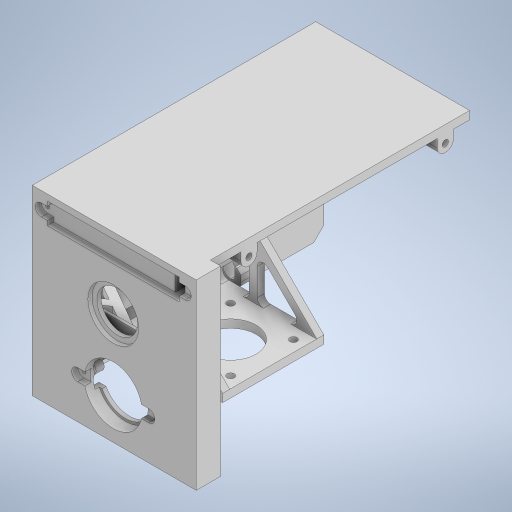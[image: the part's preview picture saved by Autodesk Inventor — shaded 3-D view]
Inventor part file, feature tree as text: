
AUTODESK INVENTOR PART (.ipt)
format: ipt  version: 2023 (Build 270158000, 158)  size: 762,368 bytes
history: native  units: mm
features: extrude x30, sketch x27, fillet x8, chamfer x7, other x6, mirror x2, revolve x2
ambient origin geometry x8: Origin, YZ Plane, XZ Plane, XY Plane, X Axis, Y Axis, Z Axis, Center Point
bodies: Body1 (feature_tree)
feature tree (82):
  other  "솔리드1"
  sketch  "스케치1"
  extrude  "돌출1"  Depth=90.0mm
  extrude  "돌출2"  Depth=140.0mm
  extrude  "돌출3"  Depth=4.0mm TaperAngle=0.0deg
  extrude  "돌출5"  Depth=72.0mm TaperAngle=0.0deg
  extrude  "돌출6"  Depth=4.0mm
  other  "작업 평면1"
  mirror  "미러1"
  extrude  "돌출7"  Depth=4.0mm
  extrude  "돌출8"  Depth=10.0mm
  extrude  "돌출9"  Depth=10.0mm
  extrude  "돌출10"  Depth=10.0mm
  extrude  "돌출11"  Depth=10.0mm
  sketch  "스케치11"
  extrude  "돌출12"  Depth=4.0mm
  extrude  "돌출13"  Depth=10.0mm TaperAngle=0.0deg
  extrude  "돌출14"  Depth=6.0mm
  chamfer  "모따기2"  Distance=36.0mm
  chamfer  "모따기3"  Distance=8.0mm
  extrude  "돌출15"  Depth=50.0mm
  fillet  "모깎기2"  Radius=10.0mm
  other  "작업 평면2"
  sketch  "스케치17"
  revolve  "회전1"
  revolve  "회전2"
  extrude  "돌출16"  Depth=46.0mm TaperAngle=0.0deg
  sketch  "스케치19"
  extrude  "돌출17"  Depth=30.0mm
  extrude  "돌출18"  TaperAngle=30.0deg  [1 undecoded]
  extrude  "돌출19"  Depth=4.0mm
  fillet  "모깎기3"  Radius=2.0mm
  other  "작업 평면3"
  extrude  "돌출20"  Depth=2.0mm
  extrude  "돌출21"  Depth=4.0mm TaperAngle=0.0deg
  extrude  "돌출22"  Depth=2.0mm
  other  "작업 평면4"
  fillet  "모깎기4"  Radius=40.0mm
  mirror  "미러2"
  chamfer  "모따기4"  Distance=20.0mm
  extrude  "돌출23"  Depth=20.0mm
  extrude  "돌출24"  Depth=36.0mm
  chamfer  "모따기5"  Distance=20.0mm
  extrude  "돌출25"  Depth=20.0mm TaperAngle=0.0deg
  chamfer  "모따기6"  Distance=5.0mm
  extrude  "돌출26"  Depth=5.0mm TaperAngle=0.0deg
  fillet  "모깎기5"  Radius=65.0mm
  extrude  "돌출27"  Depth=10.5mm
  chamfer  "모따기7"  Distance=3.0mm
  extrude  "돌출28"  Depth=3.0mm TaperAngle=0.0deg
  fillet  "모깎기6"  Radius=2.0mm
  other  "작업 평면5"
  extrude  "돌출29"  Depth=6.0mm
  fillet  "모깎기7"  Radius=3.0mm
  fillet  "모깎기8"  Radius=10.0mm
  chamfer  "모따기8"  Distance=55.0mm
  fillet  "모깎기9"  Radius=10.0mm
  extrude  "돌출30"  Depth=1.0mm TaperAngle=45.0deg
  extrude  "돌출31"  Depth=1.0mm TaperAngle=45.0deg
  sketch  "스케치2"
  sketch  "스케치3"
  sketch  "스케치4"
  sketch  "스케치5"
  sketch  "스케치6"
  sketch  "스케치7"
  sketch  "스케치9"
  sketch  "스케치10"
  sketch  "스케치12"
  sketch  "스케치14"
  sketch  "스케치18"
  sketch  "스케치20"
  sketch  "스케치21"
  sketch  "스케치22"
  sketch  "스케치25"
  sketch  "스케치26"
  sketch  "스케치27"
  sketch  "스케치28"
  sketch  "스케치29"
  sketch  "스케치30"
  sketch  "스케치31"
  sketch  "스케치33"
  sketch  "스케치34"
note: 1 required parameter value undecoded (feature->parameter linkage not recoverable at this tier; creation-order binding heuristic only, values carry confidence <= 0.55)
